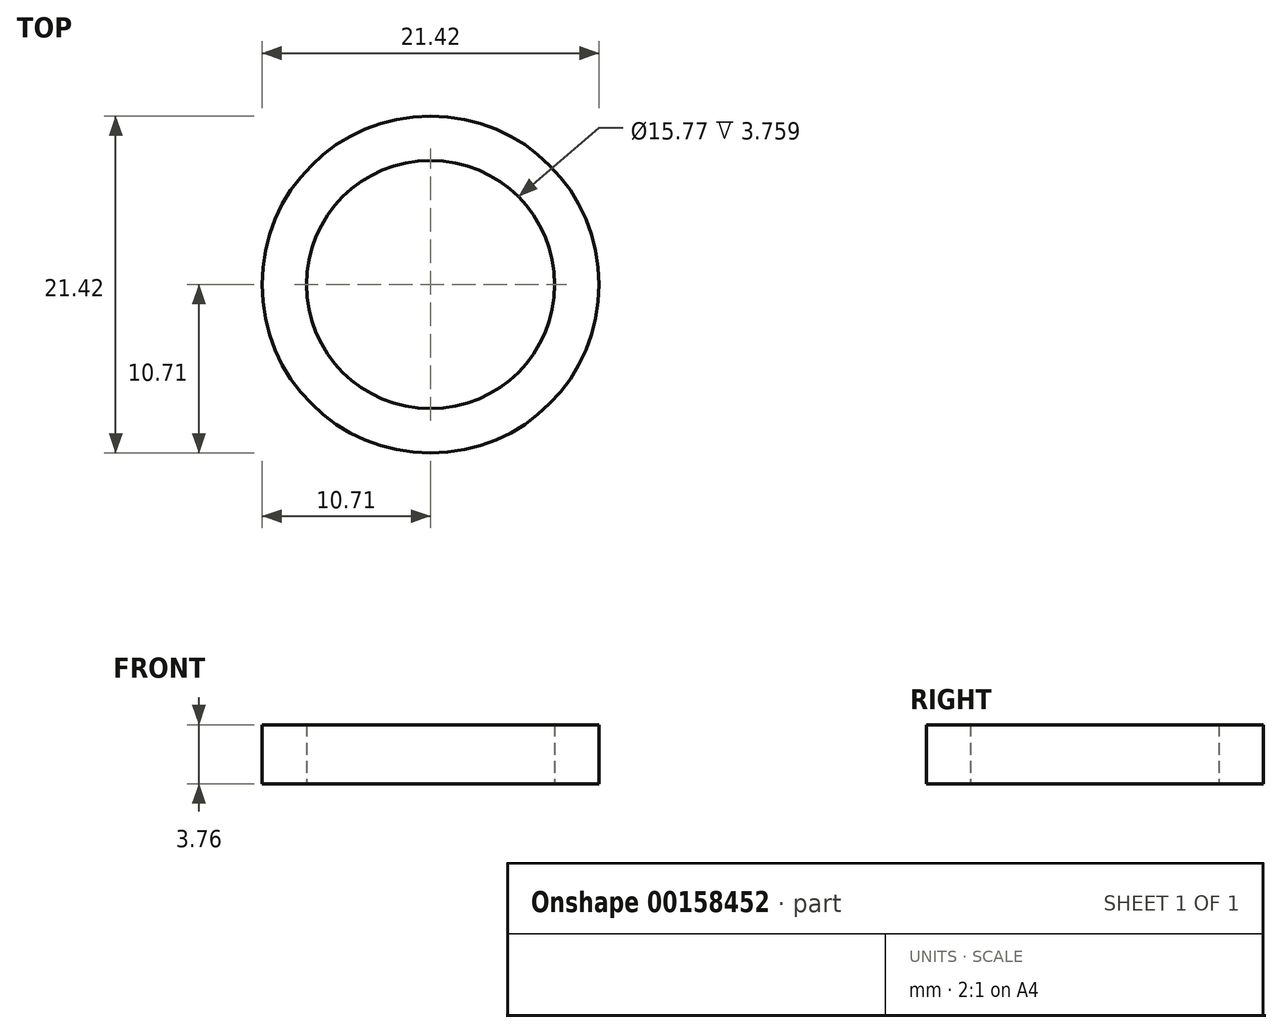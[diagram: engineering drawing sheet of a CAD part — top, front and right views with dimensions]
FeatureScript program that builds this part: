
annotation { "Feature Type Name" : "Feature", "Feature Type Description" : "" }
export const myFeature = defineFeature(function(context is Context, id is Id, definition is map)
    precondition{}
    {
        {
            var Q0;
            Q0=qCreatedBy(makeId("Top.planeOp"),FACE);
            var sketch = newSketch(context, id + "F0", { "sketchPlane" : qUnion([Q0])});
            skCircle(sketch, "E0", {"center": v(0, 0) * mm, "radius": 10.7 * mm});
            skCircle(sketch, "E1", {"center": v(0, 0) * mm, "radius": 7.89 * mm});
            skSolve(sketch);
        }
        {
            var Q0;
            Q0=makeQuery(id+"F0.imprint","IMPRINT",FACE,{"disambiguationData":[TD([[makeQuery(id+"F0.imprint","IMPRINT",EDGE,{"derivedFrom":sQuery(id+"F0.wireOp",EDGE,"E0")}),1.0]])]});
            extrude(context, id + "F1", {"entities" : qUnion([Q0]), "depth" : 3.76 * mm});
        }
    });
